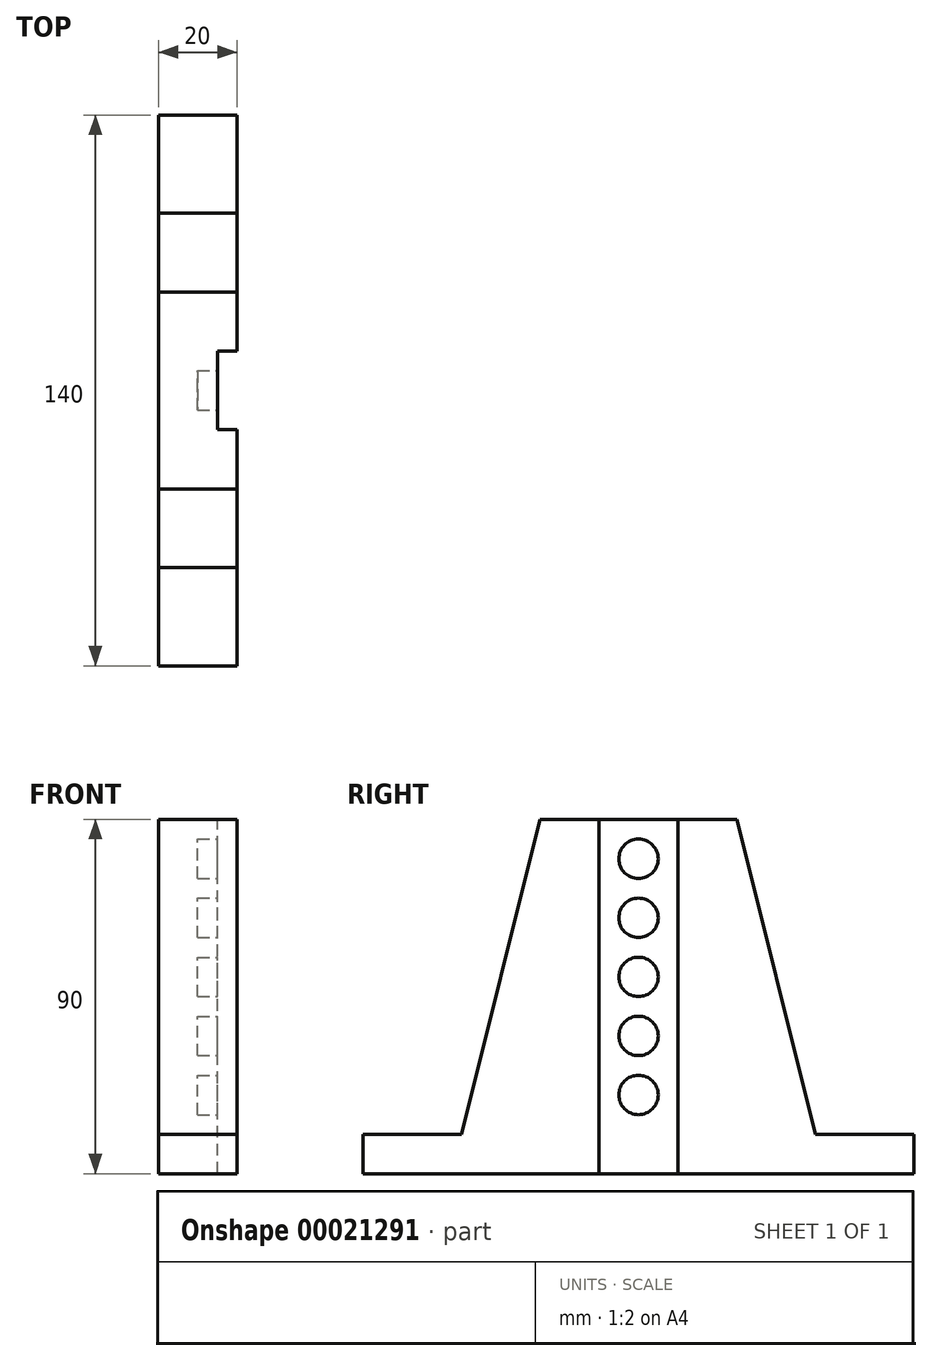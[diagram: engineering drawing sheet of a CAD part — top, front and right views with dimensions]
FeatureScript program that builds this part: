
annotation { "Feature Type Name" : "Feature", "Feature Type Description" : "" }
export const myFeature = defineFeature(function(context is Context, id is Id, definition is map)
    precondition{}
    {
        {
            var Q0;
            Q0=qCreatedBy(makeId("Right.planeOp"),FACE);
            var sketch = newSketch(context, id + "F0", { "sketchPlane" : qUnion([Q0])});
            skLineSegment(sketch, "E0", {"start": v(0, 0) * mm, "end": v(70, 0) * mm});
            skLineSegment(sketch, "E1", {"start": v(25, 90) * mm, "end": v(0, 90) * mm});
            skLineSegment(sketch, "E2", {"start": v(0, 90) * mm, "end": v(0, 0) * mm, "construction": true});
            skLineSegment(sketch, "E3.MirrorCS", {"start": v(-25, 90) * mm, "end": v(0, 90) * mm});
            skLineSegment(sketch, "E4.MirrorCS", {"start": v(0, 0) * mm, "end": v(-70, 0) * mm});
            skLineSegment(sketch, "E5", {"start": v(70, 0) * mm, "end": v(70, 10) * mm});
            skLineSegment(sketch, "E6.MirrorCS", {"start": v(-70, 0) * mm, "end": v(-70, 10) * mm});
            skLineSegment(sketch, "E7", {"start": v(70, 10) * mm, "end": v(45, 10) * mm});
            skLineSegment(sketch, "E8.MirrorCS", {"start": v(-70, 10) * mm, "end": v(-45, 10) * mm});
            skLineSegment(sketch, "E9", {"start": v(25, 90) * mm, "end": v(45, 10) * mm});
            skLineSegment(sketch, "E10.MirrorCS", {"start": v(-25, 90) * mm, "end": v(-45, 10) * mm});
            skSolve(sketch);
        }
        {
            var Q0;
            Q0=qSketchRegion(id+"F0",true);
            extrude(context, id + "F1", {"entities" : qUnion([Q0]), "depth" : 30 * mm});
        }
        {
            var Q0;
            Q0=makeQuery(id+"F1.opExtrude","CAP_FACE",FACE,{"disambiguationData":[OSD([sQuery(id+"F0.wireOp",EDGE,"E0"),sQuery(id+"F0.wireOp",EDGE,"82b1d3a8-3a79-482d-8b82-a68abf009b88"),sQuery(id+"F0.wireOp",EDGE,"E1"),sQuery(id+"F0.wireOp",EDGE,"E3.MirrorCS"),sQuery(id+"F0.wireOp",EDGE,"b3afdc77-ff44-48c9-8239-d7ec55101b530.MirrorCS"),sQuery(id+"F0.wireOp",EDGE,"E4.MirrorCS")])],"isStart":false});
            var sketch = newSketch(context, id + "F2", { "sketchPlane" : qUnion([Q0])});
            skLineSegment(sketch, "E11", {"start": v(0, 0) * mm, "end": v(0, 90) * mm, "construction": true});
            skCircle(sketch, "E12", {"center": v(0, 20) * mm, "radius": 5 * mm});
            skCircle(sketch, "E13.0.1.0", {"center": v(0, 35) * mm, "radius": 5 * mm});
            skCircle(sketch, "E13.0.2.0", {"center": v(0, 50) * mm, "radius": 5 * mm});
            skCircle(sketch, "E13.0.3.0", {"center": v(0, 65) * mm, "radius": 5 * mm});
            skLineSegment(sketch, "E13.direction1", {"start": v(0, 20) * mm, "end": v(25, 20) * mm, "construction": true});
            skLineSegment(sketch, "E13.direction2", {"start": v(0, 20) * mm, "end": v(0, 35) * mm, "construction": true});
            skCircle(sketch, "E14.0.0.4", {"center": v(0, 80) * mm, "radius": 5 * mm});
            skSolve(sketch);
        }
        {
            var Q0;
            Q0=qSketchRegion(id+"F2",true);
            extrude(context, id + "F3", {"entities" : qUnion([Q0]), "operationType" : NewBodyOperationType.REMOVE, "oppositeDirection" : true, "depth" : 10 * mm});
        }
        {
            var Q0;
            Q0=makeQuery(id+"F1.opExtrude","CAP_FACE",FACE,{"disambiguationData":[OSD([sQuery(id+"F0.wireOp",EDGE,"E0"),sQuery(id+"F0.wireOp",EDGE,"82b1d3a8-3a79-482d-8b82-a68abf009b88"),sQuery(id+"F0.wireOp",EDGE,"E1"),sQuery(id+"F0.wireOp",EDGE,"E3.MirrorCS"),sQuery(id+"F0.wireOp",EDGE,"b3afdc77-ff44-48c9-8239-d7ec55101b530.MirrorCS"),sQuery(id+"F0.wireOp",EDGE,"E4.MirrorCS")])],"isStart":false});
            var sketch = newSketch(context, id + "F4", { "sketchPlane" : qUnion([Q0])});
            skLineSegment(sketch, "E15.rect.bottom", {"start": v(10, 0) * mm, "end": v(-10, 0) * mm});
            skLineSegment(sketch, "E15.rect.top", {"start": v(10, 90) * mm, "end": v(-10, 90) * mm});
            skLineSegment(sketch, "E15.rect.left", {"start": v(10, 0) * mm, "end": v(10, 90) * mm});
            skLineSegment(sketch, "E15.rect.right", {"start": v(-10, 0) * mm, "end": v(-10, 90) * mm});
            skPoint(sketch, "E15.rect.middle", {"position": v(0, 45) * mm});
            skSolve(sketch);
        }
        {
            var Q0;
            Q0=qSketchRegion(id+"F4",true);
            extrude(context, id + "F5", {"entities" : qUnion([Q0]), "operationType" : NewBodyOperationType.REMOVE, "oppositeDirection" : true, "depth" : 5 * mm});
        }
        {
            var Q0;
            {var subQ0=sQuery(id+"F0.wireOp",EDGE,"E0");var subQ1=sQuery(id+"F0.wireOp",EDGE,"E1");var subQ2=sQuery(id+"F0.wireOp",EDGE,"E3.MirrorCS");var subQ3=sQuery(id+"F0.wireOp",EDGE,"E4.MirrorCS");var subQ4=sQuery(id+"F0.wireOp",EDGE,"E6.MirrorCS");var subQ5=sQuery(id+"F0.wireOp",EDGE,"E8.MirrorCS");var subQ6=sQuery(id+"F0.wireOp",EDGE,"E10.MirrorCS");Q0=makeQuery(id+"F5.boolean.opBoolean","SPLIT",FACE,{"disambiguationData":[TD([makeQuery(id+"F1.opExtrude","SWEPT_FACE",FACE,{"disambiguationData":[OSD([subQ4])]})])],"derivedFrom":makeQuery(id+"F1.opExtrude","CAP_FACE",FACE,{"disambiguationData":[OSD([subQ0,subQ1,subQ2,subQ3,sQuery(id+"F0.wireOp",EDGE,"E5"),subQ4,sQuery(id+"F0.wireOp",EDGE,"E7"),subQ5,sQuery(id+"F0.wireOp",EDGE,"E9"),subQ6])],"isStart":false})});}
            cPlane(context, id + "F6", {"entities" : qUnion([Q0]), "cplaneType" : CPlaneType.OFFSET, "offset" : 10 * mm, "oppositeDirection" : true, "width" : 150 * mm, "height" : 150 * mm});
        }
        {
            var Q0;
            Q0=makeQuery(id+"F1.opExtrude","CAP_FACE",FACE,{"disambiguationData":[OSD([sQuery(id+"F0.wireOp",EDGE,"E0"),sQuery(id+"F0.wireOp",EDGE,"E1"),sQuery(id+"F0.wireOp",EDGE,"E3.MirrorCS"),sQuery(id+"F0.wireOp",EDGE,"E4.MirrorCS"),sQuery(id+"F0.wireOp",EDGE,"E5"),sQuery(id+"F0.wireOp",EDGE,"E6.MirrorCS"),sQuery(id+"F0.wireOp",EDGE,"E7"),sQuery(id+"F0.wireOp",EDGE,"E8.MirrorCS"),sQuery(id+"F0.wireOp",EDGE,"E9"),sQuery(id+"F0.wireOp",EDGE,"E10.MirrorCS")])],"isStart":true});
            var Q1;
            Q1=qCreatedBy(id+"F6.planeOp",FACE);
            extrude(context, id + "F7", {"entities" : qUnion([Q0]), "operationType" : NewBodyOperationType.REMOVE, "oppositeDirection" : true, "endBoundEntityFace" : qUnion([Q1]), "depth" : 10 * mm});
        }
    });
